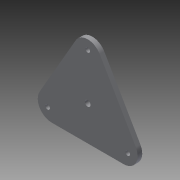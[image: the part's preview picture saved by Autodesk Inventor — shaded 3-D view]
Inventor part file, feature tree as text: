
AUTODESK INVENTOR PART (.ipt)
format: ipt  version: 2013 (Build 170138000, 138)  size: 89,600 bytes
history: native  units: in
note: dims shown in document units (in); Inventor stores cm internally (conversion verified against a paired STEP export)
features: extrude x1, fillet x1, sketch x1
ambient origin geometry x8: Origin, YZ Plane, XZ Plane, XY Plane, X Axis, Y Axis, Z Axis, Center Point
bodies: Solid1 (feature_tree)
feature tree (3):
  extrude  "Extrusion1"  Depth=0.25in
  fillet  "Fillet1"  Radius=2.5in
  sketch  "Sketch2"  dims[d0=0.3125in d1=0.25in d2=2.5in d3=1.1811in d5=360.0deg d8=0.5in d9=0.5in d10=0.5in d11=0.25in d12=0.0in d13=0.75in]
